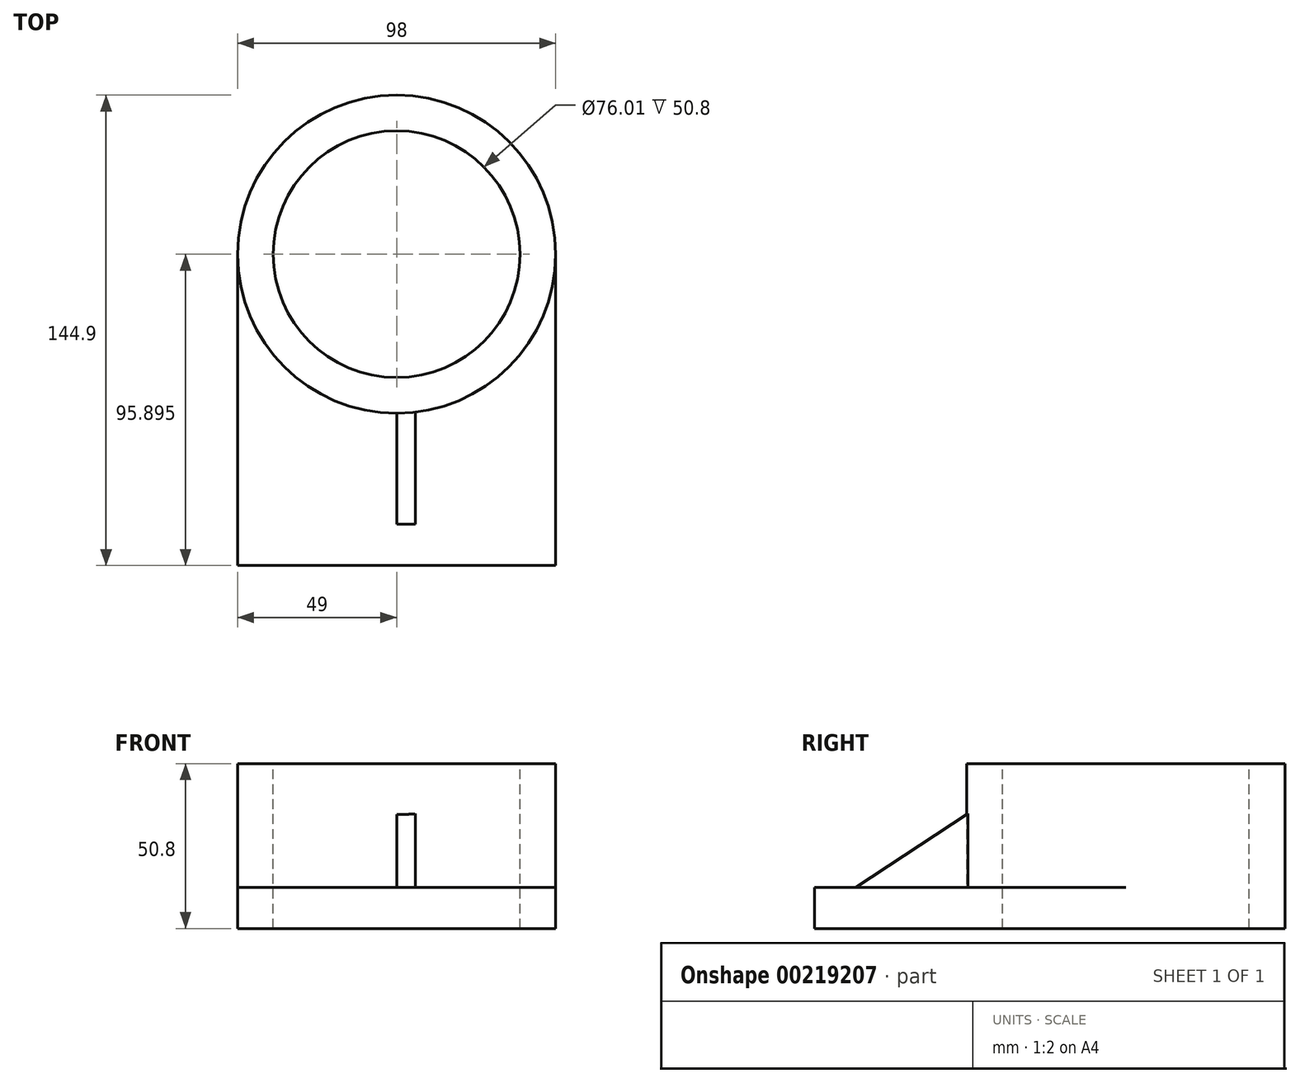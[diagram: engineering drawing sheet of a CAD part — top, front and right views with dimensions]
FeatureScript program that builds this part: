
annotation { "Feature Type Name" : "Feature", "Feature Type Description" : "" }
export const myFeature = defineFeature(function(context is Context, id is Id, definition is map)
    precondition{}
    {
        {
            var Q0;
            Q0=qCreatedBy(makeId("Top.planeOp"),FACE);
            var sketch = newSketch(context, id + "F0", { "sketchPlane" : qUnion([Q0])});
            skLineSegment(sketch, "E0.top", {"start": v(49, -47.95) * mm, "end": v(-49, -47.95) * mm});
            skLineSegment(sketch, "E0.left", {"start": v(49, 47.95) * mm, "end": v(49, -47.95) * mm});
            skLineSegment(sketch, "E0.right", {"start": v(-49, 47.95) * mm, "end": v(-49, -47.95) * mm});
            skPoint(sketch, "E0.middle", {"position": v(0, 0) * mm});
            skCircle(sketch, "E1", {"center": v(0, 47.95) * mm, "radius": 49 * mm});
            skSolve(sketch);
        }
        {
            var Q0;
            Q0=makeQuery(id+"F0.imprint","IMPRINT",FACE,{"disambiguationData":[TD([[makeQuery(id+"F0.imprint","IMPRINT",EDGE,{"derivedFrom":sQuery(id+"F0.wireOp",EDGE,"E0.top")}),-1.0]])]});
            extrude(context, id + "F1", {"entities" : qUnion([Q0]), "depth" : 12.7 * mm});
        }
        {
            var Q0;
            Q0=qCreatedBy(makeId("Top.planeOp"),FACE);
            var sketch = newSketch(context, id + "F2", { "sketchPlane" : qUnion([Q0])});
            skArc(sketch, "E2.0.0", {"start": v(49, 47.95) * mm, "mid": v(0, -1.06) * mm, "end": v(-49, 47.95) * mm});
            skLineSegment(sketch, "E2.0.1", {"start": v(-49, 47.95) * mm, "end": v(-49, -47.95) * mm});
            skLineSegment(sketch, "E2.0.2", {"start": v(-49, -47.95) * mm, "end": v(49, -47.95) * mm});
            skLineSegment(sketch, "E2.0.3", {"start": v(49, -47.95) * mm, "end": v(49, 47.95) * mm});
            skCircle(sketch, "E3", {"center": v(0, 47.95) * mm, "radius": 49 * mm});
            skSolve(sketch);
        }
        {
            var Q0;
            {var subQ0=sQuery(id+"F2.wireOp",EDGE,"E3");var subQ1=makeQuery(id+"F2.imprint","INTERSECT",VERTEX,{"derivedFrom":[sQuery(id+"F2.wireOp",EDGE,"E2.0.1"),subQ0]});Q0=makeQuery(id+"F2.imprint","IMPRINT",FACE,{"disambiguationData":[TD([[makeQuery(id+"F2.imprint","IMPRINT",EDGE,{"disambiguationData":[TD([[subQ1,1.0]])],"derivedFrom":subQ0}),1.0]])]});}
            extrude(context, id + "F3", {"entities" : qUnion([Q0]), "operationType" : NewBodyOperationType.ADD, "depth" : 50.8 * mm});
        }
        {
            var Q0;
            Q0=makeQuery(id+"F3.opExtrude","CAP_FACE",FACE,{"disambiguationData":[OSD([sQuery(id+"F2.wireOp",EDGE,"E3")])],"isStart":false});
            var sketch = newSketch(context, id + "F4", { "sketchPlane" : qUnion([Q0])});
            skCircle(sketch, "E4.0", {"center": v(0, 47.95) * mm, "radius": 49 * mm});
            skCircle(sketch, "E5", {"center": v(0, 47.95) * mm, "radius": 38 * mm});
            skSolve(sketch);
        }
        {
            var Q0;
            Q0=makeQuery(id+"F4.imprint","IMPRINT",FACE,{"disambiguationData":[TD([[makeQuery(id+"F4.imprint","IMPRINT",EDGE,{"derivedFrom":sQuery(id+"F4.wireOp",EDGE,"E5")}),1.0]])]});
            extrude(context, id + "F5", {"entities" : qUnion([Q0]), "operationType" : NewBodyOperationType.REMOVE, "endBound" : BoundingType.THROUGH_ALL, "oppositeDirection" : true, "depth" : 25.4 * mm});
        }
        {
            var Q0;
            Q0=makeQuery(id+"F1.opExtrude","SWEPT_FACE",FACE,{"disambiguationData":[OSD([sQuery(id+"F0.wireOp",EDGE,"E0.left")])]});
            cPlane(context, id + "F6", {"entities" : qUnion([Q0]), "cplaneType" : CPlaneType.OFFSET, "offset" : 25.4 * mm, "oppositeDirection" : true, "width" : 152.4 * mm, "height" : 152.4 * mm});
        }
        {
            var Q0;
            Q0=qCreatedBy(id+"F6.planeOp",FACE);
            var Q1;
            Q1=qCreatedBy(makeId("Origin.pointOp"),VERTEX);
            cPlane(context, id + "F7", {"entities" : qUnion([Q0, Q1]), "cplaneType" : CPlaneType.PLANE_POINT, "offset" : 25.4 * mm, "width" : 152.4 * mm, "height" : 152.4 * mm});
        }
        {
            var Q0;
            Q0=qCreatedBy(id+"F7.planeOp",FACE);
            var sketch = newSketch(context, id + "F8", { "sketchPlane" : qUnion([Q0])});
            skLineSegment(sketch, "E6", {"start": v(-35.21, 12.7) * mm, "end": v(0, 35.8) * mm});
            skLineSegment(sketch, "E7", {"start": v(0, 35.8) * mm, "end": v(0, 12.7) * mm});
            skLineSegment(sketch, "E8", {"start": v(0, 12.7) * mm, "end": v(-35.21, 12.7) * mm});
            skSolve(sketch);
        }
        {
            var Q0;
            Q0 = qSketchRegion(id + "F8", true);
            extrude(context, id + "F9", {"entities" : qUnion([Q0]), "operationType" : NewBodyOperationType.ADD, "depth" : 5.84 * mm});
        }
    });
